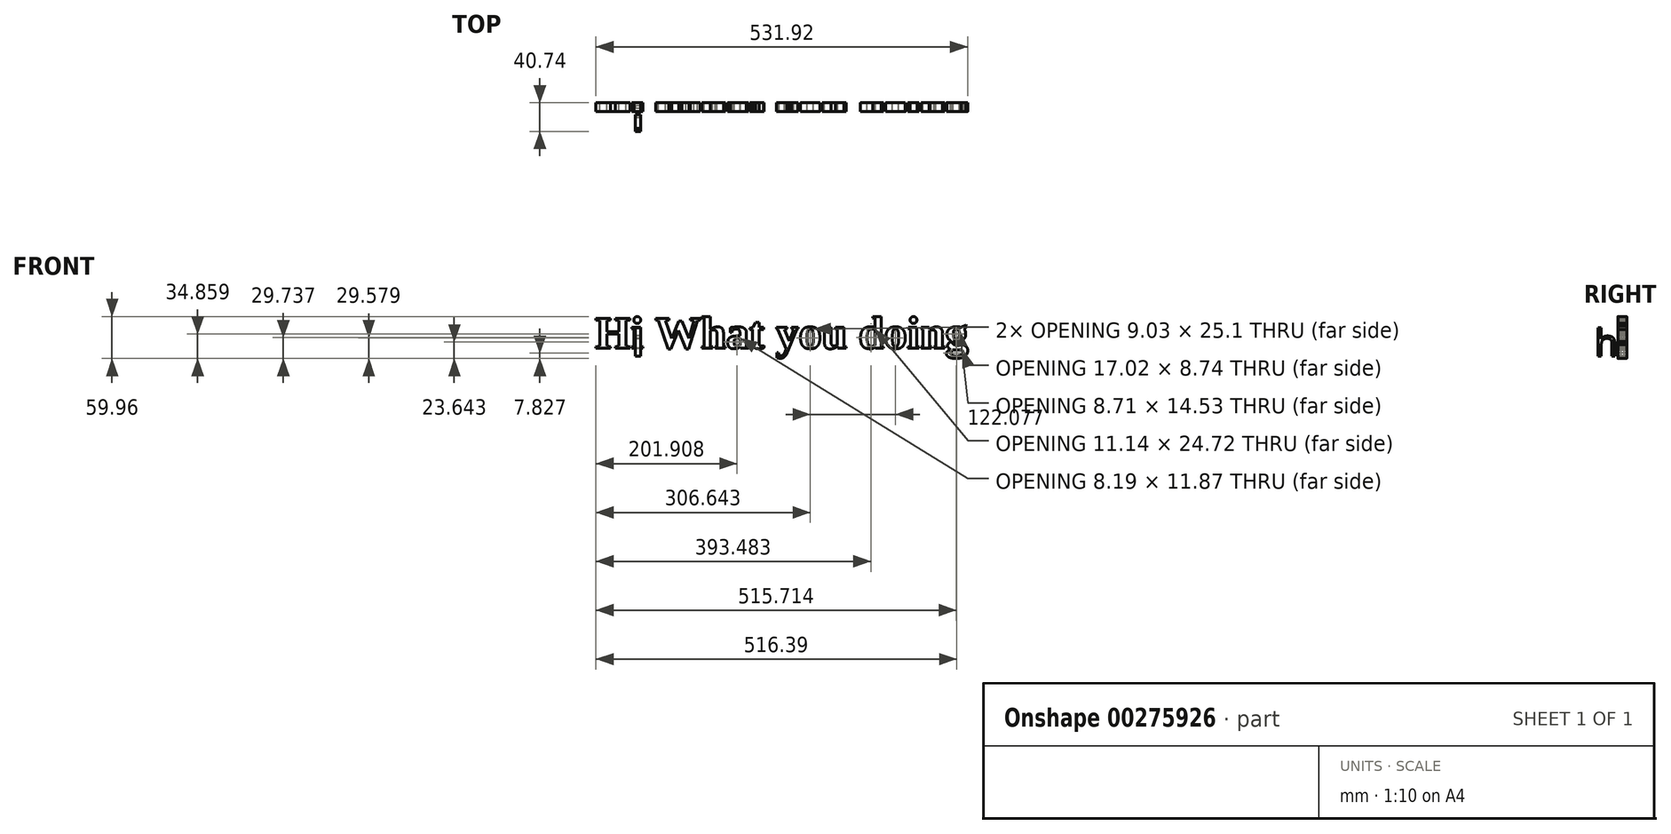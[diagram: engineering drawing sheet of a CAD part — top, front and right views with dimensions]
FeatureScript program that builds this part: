
annotation { "Feature Type Name" : "Feature", "Feature Type Description" : "" }
export const myFeature = defineFeature(function(context is Context, id is Id, definition is map)
    precondition{}
    {
        {
            var Q0;
            Q0=qCreatedBy(makeId("Front.planeOp"),FACE);
            var sketch = newSketch(context, id + "F0", { "sketchPlane" : qUnion([Q0])});
            skText(sketch, "E0", { "text": "Hi What you doing", "fontName": "Tinos-Bold.ttf"});
            const initialGuessF0  = {"E0": [-0.05752, 0.01106, 1, 0, 0.0472]};
            skSetInitialGuess(sketch, initialGuessF0);
            skSolve(sketch);
        }
        {
            var Q0;
            Q0=qSketchRegion(id+"F0",true);
            var Q1;
            Q1=qSketchRegion(id+"FX9OlSxoKtIA36Z_16",true);
            extrude(context, id + "F1", {"entities" : qUnion([Q0, Q1]), "depth" : 12.7 * mm});
        }
        {
            var Q0;
            Q0=qCreatedBy(makeId("Right.planeOp"),FACE);
            var sketch = newSketch(context, id + "F2", { "sketchPlane" : qUnion([Q0])});
            skText(sketch, "E1", { "text": "hi\n", "fontName": "OpenSans-Regular.ttf"});
            const initialGuessF2  = {"E1": [-0.0453, 0, 1, 0, 0.03822]};
            skSetInitialGuess(sketch, initialGuessF2);
            skSolve(sketch);
        }
        {
            var Q0;
            Q0=qSketchRegion(id+"F2",true);
            extrude(context, id + "F3", {"entities" : qUnion([Q0]), "operationType" : NewBodyOperationType.ADD, "depth" : 7.62 * mm});
        }
    });
